# Revit family: 851-45-001-DN50-200
name_source: partatom
category: Pipe Accessories
units: mm (PartAtom-declared; Revit-internal decimal feet)

## family parameters
Always vertical = Yes
Cut with Voids When Loaded = No
Part Type = Valve - Breaks Into
Round Connector Dimension = Use Diameter
Shared = No
Work Plane-Based = No

## types (6) — shared parameters
DN050_PN10/16 = 851-050-45-122000
DN080_PN10/16 = 851-080-45-122000
DN100_PN10/16 = 851-100-45-122000
DN150_PN10/16 = 851-150-45-122000
DN200_PN10 = 851-200-45-022000
DN200_PN16 = 851-200-45-122000
Description_ = AVK DOUBLE ORIFICE AIR RELIEF VALVE
Fillet_thickness = 10 mm  [stored 0.0328084 ft]
Search_table = 851-45-001-DN50-200
URL product pages = https://www.avkvalves.com

## per-type parameters (varying)
| type | Body_dia | Body_dia_1 | Body_dia_2 | Body_height | Body_height_1 | Body_height_2 | Body_height_3 | Bonnet_flange | Bonnet_flange_2 | Bonnet_height | Bonnet_length | D | DN | D_ref | Flange_dia | H3 | RF_dia | Top_ref | W | W1 | W1_ref | W6 | W_ref | W_ref_2 |
| DN050_PN10/16 | 57 mm  [stored 0.187008 ft] | 32 mm | 57 mm  [stored 0.187008 ft] | 204 mm | 88 mm  [stored 0.288714 ft] | 135 mm  [stored 0.442913 ft] | 142 mm | 13 mm | 19 mm  [stored 0.062336 ft] | 79 mm | 140 mm  [stored 0.459318 ft] | 50 mm  [stored 0.164042 ft] | 50 mm  [stored 0.164042 ft] | 25 mm  [stored 0.082021 ft] | 83 mm  [stored 0.27231 ft] | 277 mm | 51 mm  [stored 0.167323 ft] | 217 mm | 165 mm | 82 mm  [stored 0.269029 ft] | 71 mm | 220 mm | 138 mm  [stored 0.452756 ft] | 151 mm |
| DN080_PN10/16 | 57 mm  [stored 0.187008 ft] | 46 mm | 57 mm  [stored 0.187008 ft] | 204 mm | 100 mm  [stored 0.328084 ft] | 120 mm  [stored 0.393701 ft] | 126 mm  [stored 0.413386 ft] | 13 mm | 19 mm  [stored 0.062336 ft] | 79 mm | 140 mm  [stored 0.459318 ft] | 80 mm  [stored 0.262467 ft] | 80 mm  [stored 0.262467 ft] | 40 mm  [stored 0.131234 ft] | 100 mm  [stored 0.328084 ft] | 277 mm | 69 mm  [stored 0.226378 ft] | 217 mm | 165 mm | 82 mm  [stored 0.269029 ft] | 71 mm | 220 mm | 138 mm  [stored 0.452756 ft] | 151 mm |
| DN100_PN10/16 | 80 mm  [stored 0.262467 ft] | 58 mm | 58 mm | 204 mm | 51 mm  [stored 0.167323 ft] | 64 mm  [stored 0.209974 ft] | 67 mm | 13 mm | 25 mm  [stored 0.082021 ft] | 80 mm  [stored 0.262467 ft] | 140 mm  [stored 0.459318 ft] | 100 mm  [stored 0.328084 ft] | 100 mm  [stored 0.328084 ft] | 50 mm  [stored 0.164042 ft] | 110 mm  [stored 0.360892 ft] | 283 mm | 79 mm | 217 mm | 205 mm | 102 mm  [stored 0.334646 ft] | 89 mm | 248 mm | 171 mm | 188 mm |
| DN150_PN10/16 | 100 mm  [stored 0.328084 ft] | 83 mm  [stored 0.27231 ft] | 63 mm  [stored 0.206693 ft] | 250 mm | 57 mm  [stored 0.187008 ft] | 70 mm  [stored 0.229659 ft] | 74 mm | 20 mm  [stored 0.0656168 ft] | 28 mm  [stored 0.0918635 ft] | 72 mm  [stored 0.23622 ft] | 153 mm | 150 mm | 150 mm | 75 mm  [stored 0.246063 ft] | 143 mm | 345 mm | 106 mm  [stored 0.347769 ft] | 270 mm | 255 mm | 127 mm | 110 mm  [stored 0.360892 ft] | 286 mm | 213 mm | 234 mm |
| DN200_PN10 | 100 mm  [stored 0.328084 ft] | 83 mm  [stored 0.27231 ft] | 63 mm  [stored 0.206693 ft] | 250 mm | 57 mm  [stored 0.187008 ft] | 70 mm  [stored 0.229659 ft] | 74 mm | 20 mm  [stored 0.0656168 ft] | 28 mm  [stored 0.0918635 ft] | 72 mm  [stored 0.23622 ft] | 153 mm | 150 mm | 200 mm | 75 mm  [stored 0.246063 ft] | 170 mm | 345 mm | 134 mm | 270 mm | 255 mm | 127 mm | 110 mm  [stored 0.360892 ft] | 286 mm | 213 mm | 234 mm |
| DN200_PN16 | 100 mm  [stored 0.328084 ft] | 83 mm  [stored 0.27231 ft] | 63 mm  [stored 0.206693 ft] | 250 mm | 57 mm  [stored 0.187008 ft] | 70 mm  [stored 0.229659 ft] | 74 mm | 20 mm  [stored 0.0656168 ft] | 28 mm  [stored 0.0918635 ft] | 72 mm  [stored 0.23622 ft] | 153 mm | 150 mm | 200 mm | 75 mm  [stored 0.246063 ft] | 170 mm | 345 mm | 134 mm | 270 mm | 255 mm | 127 mm | 110 mm  [stored 0.360892 ft] | 286 mm | 213 mm | 234 mm |

note: [stored X ft] marks values corroborated as IEEE doubles in the binary element streams (Revit-internal decimal feet)

## geometry (parser evidence)
native form markers: Sweep x4
no freeform markers — native parametric forms only
